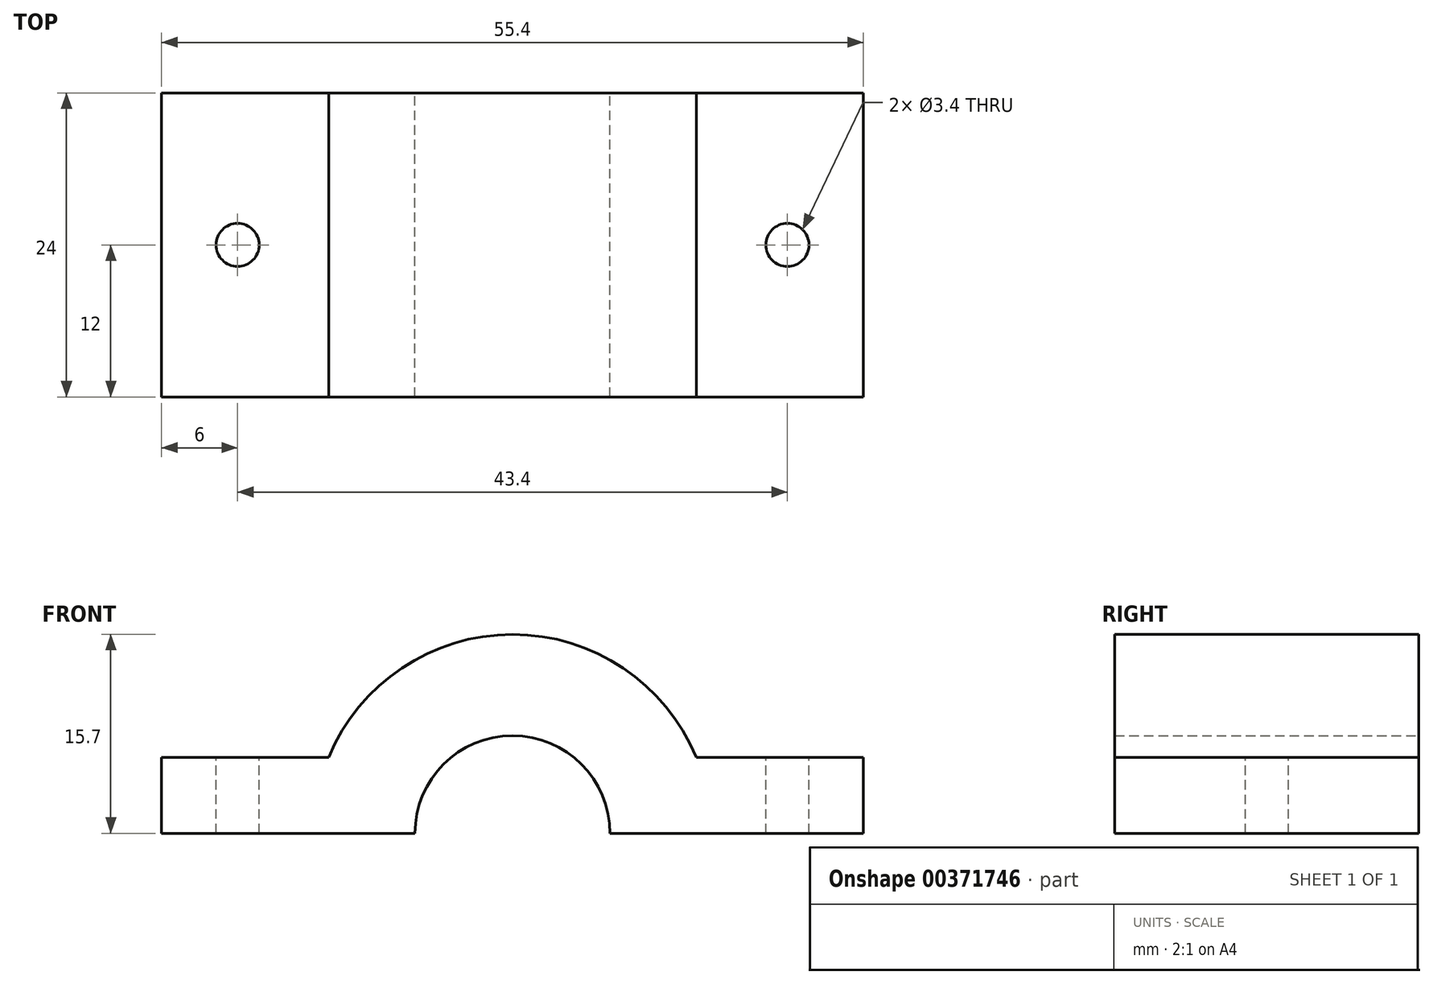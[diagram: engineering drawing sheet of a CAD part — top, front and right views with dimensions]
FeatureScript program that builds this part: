
annotation { "Feature Type Name" : "Feature", "Feature Type Description" : "" }
export const myFeature = defineFeature(function(context is Context, id is Id, definition is map)
    precondition{}
    {
        {
            var Q0;
            Q0=qCreatedBy(makeId("Front.planeOp"),FACE);
            var sketch = newSketch(context, id + "F0", { "sketchPlane" : qUnion([Q0])});
            skArc(sketch, "E0", {"start": v(7.7, 0) * mm, "mid": v(0, 7.7) * mm, "end": v(-7.7, 0) * mm});
            skArc(sketch, "E1", {"start": v(14.5, 6) * mm, "mid": v(0, 15.7) * mm, "end": v(-14.5, 6) * mm});
            skLineSegment(sketch, "E2", {"start": v(0, 0) * mm, "end": v(-7.7, 0) * mm, "construction": true});
            skLineSegment(sketch, "E3", {"start": v(0, 0) * mm, "end": v(7.7, 0) * mm, "construction": true});
            skLineSegment(sketch, "E4", {"start": v(-7.7, 0) * mm, "end": v(-15.7, 0) * mm});
            skLineSegment(sketch, "E5", {"start": v(7.7, 0) * mm, "end": v(15.7, 0) * mm});
            skLineSegment(sketch, "E6", {"start": v(-15.7, 0) * mm, "end": v(-27.7, 0) * mm});
            skLineSegment(sketch, "E7", {"start": v(15.7, 0) * mm, "end": v(27.7, 0) * mm});
            skLineSegment(sketch, "E8", {"start": v(27.7, 0) * mm, "end": v(27.7, 6) * mm});
            skLineSegment(sketch, "E9", {"start": v(-27.7, 0) * mm, "end": v(-27.7, 6) * mm});
            skLineSegment(sketch, "E10", {"start": v(-27.7, 6) * mm, "end": v(-14.5, 6) * mm});
            skLineSegment(sketch, "E11", {"start": v(27.7, 6) * mm, "end": v(14.5, 6) * mm});
            skSolve(sketch);
        }
        {
            var Q0;
            Q0=makeQuery(id+"F0.imprint","IMPRINT",FACE,{"disambiguationData":[TD([[makeQuery(id+"F0.imprint","IMPRINT",EDGE,{"derivedFrom":sQuery(id+"F0.wireOp",EDGE,"mpgk0W1l-Rt2M-LF3O-dRHy-PWS3LamS0NjR")}),-1.0]])]});
            var Q1;
            Q1=makeQuery(id+"F0.imprint","IMPRINT",FACE,{"disambiguationData":[TD([[makeQuery(id+"F0.imprint","IMPRINT",EDGE,{"derivedFrom":sQuery(id+"F0.wireOp",EDGE,"E0")}),-1.0]])]});
            extrude(context, id + "F1", {"entities" : qUnion([Q0, Q1]), "depth" : 24 * mm});
        }
        {
            var Q0;
            Q0=makeQuery(id+"F1.opExtrude","SWEPT_FACE",FACE,{"disambiguationData":[OSD([sQuery(id+"F0.wireOp",EDGE,"E11")])]});
            var sketch = newSketch(context, id + "F2", { "sketchPlane" : qUnion([Q0])});
            skLineSegment(sketch, "E12", {"start": v(0, 0) * mm, "end": v(0, -12) * mm, "construction": true});
            skPoint(sketch, "E12.endSnap0", {"position": v(27.7, -12) * mm});
            skLineSegment(sketch, "E13", {"start": v(0, -12) * mm, "end": v(21.7, -12) * mm, "construction": true});
            skPoint(sketch, "E13.endSnap0", {"position": v(14.5, -12) * mm});
            skLineSegment(sketch, "E14", {"start": v(0, -12) * mm, "end": v(-21.7, -12) * mm, "construction": true});
            skCircle(sketch, "E15", {"center": v(-21.7, -12) * mm, "radius": 1.7 * mm});
            skCircle(sketch, "E16", {"center": v(21.7, -12) * mm, "radius": 1.7 * mm});
            skSolve(sketch);
        }
        {
            var Q0;
            Q0=makeQuery(id+"F2.imprint","IMPRINT",FACE,{"disambiguationData":[TD([[makeQuery(id+"F2.imprint","IMPRINT",EDGE,{"derivedFrom":sQuery(id+"F2.wireOp",EDGE,"E15")}),1.0]])]});
            var Q1;
            Q1=makeQuery(id+"F2.imprint","IMPRINT",FACE,{"disambiguationData":[TD([[makeQuery(id+"F2.imprint","IMPRINT",EDGE,{"derivedFrom":sQuery(id+"F2.wireOp",EDGE,"E16")}),1.0]])]});
            extrude(context, id + "F3", {"entities" : qUnion([Q0, Q1]), "operationType" : NewBodyOperationType.REMOVE, "oppositeDirection" : true, "depth" : 25 * mm});
        }
    });
